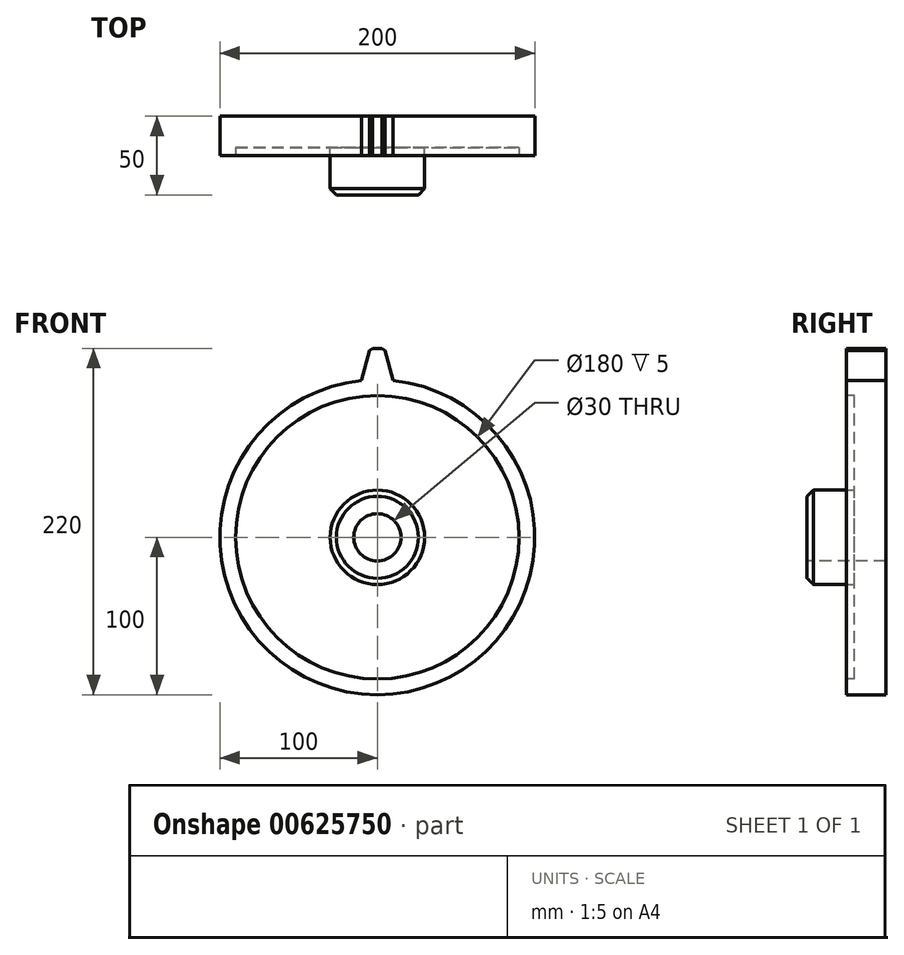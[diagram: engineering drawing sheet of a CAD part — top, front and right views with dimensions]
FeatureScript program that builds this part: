
annotation { "Feature Type Name" : "Feature", "Feature Type Description" : "" }
export const myFeature = defineFeature(function(context is Context, id is Id, definition is map)
    precondition{}
    {
        {
            var Q0;
            Q0=qCreatedBy(makeId("Front.planeOp"),FACE);
            var sketch = newSketch(context, id + "F0", { "sketchPlane" : qUnion([Q0])});
            skCircle(sketch, "E0", {"center": v(0, 0) * mm, "radius": 100 * mm});
            skSolve(sketch);
        }
        {
            var Q0;
            Q0=makeQuery(id+"F0.imprint","IMPRINT",FACE,{"disambiguationData":[TD([[makeQuery(id+"F0.imprint","IMPRINT",EDGE,{"derivedFrom":sQuery(id+"F0.wireOp",EDGE,"E0")}),1.0]])]});
            extrude(context, id + "F1", {"entities" : qUnion([Q0]), "depth" : 25 * mm, "offsetDistance" : 25 * mm});
        }
        {
            var Q0;
            Q0=makeQuery(id+"F1.opExtrude","CAP_FACE",FACE,{"disambiguationData":[OSD([sQuery(id+"F0.wireOp",EDGE,"E0")])],"isStart":false});
            var sketch = newSketch(context, id + "F2", { "sketchPlane" : qUnion([Q0])});
            skLineSegment(sketch, "E1", {"start": v(-10, 99.5) * mm, "end": v(10, 99.5) * mm});
            skLineSegment(sketch, "E2", {"start": v(10, 99.5) * mm, "end": v(4.5, 120) * mm});
            skLineSegment(sketch, "E3", {"start": v(4.5, 120) * mm, "end": v(-4.5, 120) * mm});
            skLineSegment(sketch, "E4", {"start": v(-4.5, 120) * mm, "end": v(-10, 99.5) * mm});
            skSolve(sketch);
        }
        {
            var Q0;
            {var subQ0=sQuery(id+"F2.wireOp",EDGE,"E2");Q0=makeQuery(id+"F2.imprint","IMPRINT",FACE,{"disambiguationData":[TD([[makeQuery(id+"F2.imprint","IMPRINT",EDGE,{"derivedFrom":subQ0}),1.0]])]});}
            var Q1;
            Q1 = qSketchRegion(id + "F6", true);
            var Q2;
            Q2=makeQuery(id+"F1.opExtrude","CAP_FACE",FACE,{"disambiguationData":[OSD([sQuery(id+"F0.wireOp",EDGE,"E0")])],"isStart":true});
            extrude(context, id + "F3", {"entities" : qUnion([Q0, Q1]), "operationType" : NewBodyOperationType.ADD, "endBound" : BoundingType.UP_TO_SURFACE, "oppositeDirection" : true, "depth" : 25 * mm, "endBoundEntityFace" : qUnion([Q2]), "offsetDistance" : 25 * mm});
        }
        {
            var Q0;
            Q0=makeQuery(id+"F3.opExtrude","SWEPT_EDGE",EDGE,{"disambiguationData":[OSD([sQuery(id+"F0.wireOp",EDGE,"E0"),sQuery(id+"F2.wireOp",EDGE,"E1"),sQuery(id+"F2.wireOp",EDGE,"E2")])]});
            var Q1;
            Q1=makeQuery(id+"F3.opExtrude","SWEPT_EDGE",EDGE,{"disambiguationData":[OSD([sQuery(id+"F0.wireOp",EDGE,"E0"),sQuery(id+"F2.wireOp",EDGE,"E1"),sQuery(id+"F2.wireOp",EDGE,"E4")])]});
            fillet(context, id + "F4", {"entities" : qUnion([Q0, Q1]), "radius" : 5 * mm, "tangentPropagation" : true, "allowEdgeOverflow" : false});
        }
        {
            var Q0;
            Q0=makeQuery(id+"F3.opExtrude","SWEPT_EDGE",EDGE,{"disambiguationData":[OSD([sQuery(id+"F2.wireOp",EDGE,"E2"),sQuery(id+"F2.wireOp",EDGE,"E3")])]});
            var Q1;
            Q1=makeQuery(id+"F3.opExtrude","SWEPT_EDGE",EDGE,{"disambiguationData":[OSD([sQuery(id+"F2.wireOp",EDGE,"E3"),sQuery(id+"F2.wireOp",EDGE,"E4")])]});
            chamfer(context, id + "F5", {"entities" : qUnion([Q0, Q1]), "width" : 2 * mm, "tangentPropagation" : true});
        }
        {
            var Q0;
            {var subQ0=sQuery(id+"F2.wireOp",EDGE,"E4");var subQ1=sQuery(id+"F2.wireOp",EDGE,"E3");var subQ2=sQuery(id+"F2.wireOp",EDGE,"E2");var subQ3=sQuery(id+"F0.wireOp",EDGE,"E0");Q0=makeQuery(id+"FVngeMlJqadk3JX_1.19.F3.boolean.opBoolean","MERGE",FACE,{"derivedFrom":[makeQuery(id+"FVngeMlJqadk3JX_1.18.F3.boolean.opBoolean","MERGE",FACE,{"derivedFrom":[makeQuery(id+"FVngeMlJqadk3JX_1.17.F3.boolean.opBoolean","MERGE",FACE,{"derivedFrom":[makeQuery(id+"FVngeMlJqadk3JX_1.16.F3.boolean.opBoolean","MERGE",FACE,{"derivedFrom":[makeQuery(id+"FVngeMlJqadk3JX_1.15.F3.boolean.opBoolean","MERGE",FACE,{"derivedFrom":[makeQuery(id+"FVngeMlJqadk3JX_1.14.F3.boolean.opBoolean","MERGE",FACE,{"derivedFrom":[makeQuery(id+"FVngeMlJqadk3JX_1.13.F3.boolean.opBoolean","MERGE",FACE,{"derivedFrom":[makeQuery(id+"FVngeMlJqadk3JX_1.12.F3.boolean.opBoolean","MERGE",FACE,{"derivedFrom":[makeQuery(id+"FVngeMlJqadk3JX_1.11.F3.boolean.opBoolean","MERGE",FACE,{"derivedFrom":[makeQuery(id+"FVngeMlJqadk3JX_1.10.F3.boolean.opBoolean","MERGE",FACE,{"derivedFrom":[makeQuery(id+"FVngeMlJqadk3JX_1.9.F3.boolean.opBoolean","MERGE",FACE,{"derivedFrom":[makeQuery(id+"FVngeMlJqadk3JX_1.8.F3.boolean.opBoolean","MERGE",FACE,{"derivedFrom":[makeQuery(id+"FVngeMlJqadk3JX_1.7.F3.boolean.opBoolean","MERGE",FACE,{"derivedFrom":[makeQuery(id+"FVngeMlJqadk3JX_1.6.F3.boolean.opBoolean","MERGE",FACE,{"derivedFrom":[makeQuery(id+"FVngeMlJqadk3JX_1.5.F3.boolean.opBoolean","MERGE",FACE,{"derivedFrom":[makeQuery(id+"FVngeMlJqadk3JX_1.4.F3.boolean.opBoolean","MERGE",FACE,{"derivedFrom":[makeQuery(id+"FVngeMlJqadk3JX_1.3.F3.boolean.opBoolean","MERGE",FACE,{"derivedFrom":[makeQuery(id+"FVngeMlJqadk3JX_1.2.F3.boolean.opBoolean","MERGE",FACE,{"derivedFrom":[makeQuery(id+"FVngeMlJqadk3JX_1.1.F3.boolean.opBoolean","MERGE",FACE,{"derivedFrom":[makeQuery(id+"F3.boolean.opBoolean","MERGE",FACE,{"derivedFrom":[makeQuery(id+"F1.opExtrude","CAP_FACE",FACE,{"disambiguationData":[OSD([subQ3])],"isStart":false}),makeQuery(id+"F3.opExtrude","CAP_FACE",FACE,{"disambiguationData":[OSD([subQ3,subQ2,subQ1,subQ0])],"isStart":true})]}),makeQuery(id+"FVngeMlJqadk3JX_1.1.F3.opExtrude","CAP_FACE",FACE,{"disambiguationData":[OSD([subQ3,subQ2,subQ1,subQ0])],"isStart":true})]}),makeQuery(id+"FVngeMlJqadk3JX_1.2.F3.opExtrude","CAP_FACE",FACE,{"disambiguationData":[OSD([subQ3,subQ2,subQ1,subQ0])],"isStart":true})]}),makeQuery(id+"FVngeMlJqadk3JX_1.3.F3.opExtrude","CAP_FACE",FACE,{"disambiguationData":[OSD([subQ3,subQ2,subQ1,subQ0])],"isStart":true})]}),makeQuery(id+"FVngeMlJqadk3JX_1.4.F3.opExtrude","CAP_FACE",FACE,{"disambiguationData":[OSD([subQ3,subQ2,subQ1,subQ0])],"isStart":true})]}),makeQuery(id+"FVngeMlJqadk3JX_1.5.F3.opExtrude","CAP_FACE",FACE,{"disambiguationData":[OSD([subQ3,subQ2,subQ1,subQ0])],"isStart":true})]}),makeQuery(id+"FVngeMlJqadk3JX_1.6.F3.opExtrude","CAP_FACE",FACE,{"disambiguationData":[OSD([subQ3,subQ2,subQ1,subQ0])],"isStart":true})]}),makeQuery(id+"FVngeMlJqadk3JX_1.7.F3.opExtrude","CAP_FACE",FACE,{"disambiguationData":[OSD([subQ3,subQ2,subQ1,subQ0])],"isStart":true})]}),makeQuery(id+"FVngeMlJqadk3JX_1.8.F3.opExtrude","CAP_FACE",FACE,{"disambiguationData":[OSD([subQ3,subQ2,subQ1,subQ0])],"isStart":true})]}),makeQuery(id+"FVngeMlJqadk3JX_1.9.F3.opExtrude","CAP_FACE",FACE,{"disambiguationData":[OSD([subQ3,subQ2,subQ1,subQ0])],"isStart":true})]}),makeQuery(id+"FVngeMlJqadk3JX_1.10.F3.opExtrude","CAP_FACE",FACE,{"disambiguationData":[OSD([subQ3,subQ2,subQ1,subQ0])],"isStart":true})]}),makeQuery(id+"FVngeMlJqadk3JX_1.11.F3.opExtrude","CAP_FACE",FACE,{"disambiguationData":[OSD([subQ3,subQ2,subQ1,subQ0])],"isStart":true})]}),makeQuery(id+"FVngeMlJqadk3JX_1.12.F3.opExtrude","CAP_FACE",FACE,{"disambiguationData":[OSD([subQ3,subQ2,subQ1,subQ0])],"isStart":true})]}),makeQuery(id+"FVngeMlJqadk3JX_1.13.F3.opExtrude","CAP_FACE",FACE,{"disambiguationData":[OSD([subQ3,subQ2,subQ1,subQ0])],"isStart":true})]}),makeQuery(id+"FVngeMlJqadk3JX_1.14.F3.opExtrude","CAP_FACE",FACE,{"disambiguationData":[OSD([subQ3,subQ2,subQ1,subQ0])],"isStart":true})]}),makeQuery(id+"FVngeMlJqadk3JX_1.15.F3.opExtrude","CAP_FACE",FACE,{"disambiguationData":[OSD([subQ3,subQ2,subQ1,subQ0])],"isStart":true})]}),makeQuery(id+"FVngeMlJqadk3JX_1.16.F3.opExtrude","CAP_FACE",FACE,{"disambiguationData":[OSD([subQ3,subQ2,subQ1,subQ0])],"isStart":true})]}),makeQuery(id+"FVngeMlJqadk3JX_1.17.F3.opExtrude","CAP_FACE",FACE,{"disambiguationData":[OSD([subQ3,subQ2,subQ1,subQ0])],"isStart":true})]}),makeQuery(id+"FVngeMlJqadk3JX_1.18.F3.opExtrude","CAP_FACE",FACE,{"disambiguationData":[OSD([subQ3,subQ2,subQ1,subQ0])],"isStart":true})]}),makeQuery(id+"FVngeMlJqadk3JX_1.19.F3.opExtrude","CAP_FACE",FACE,{"disambiguationData":[OSD([subQ3,subQ2,subQ1,subQ0])],"isStart":true})]});}
            var sketch = newSketch(context, id + "F6", { "sketchPlane" : qUnion([Q0])});
            skCircle(sketch, "E5", {"center": v(0, 0) * mm, "radius": 90 * mm});
            skSolve(sketch);
        }
        {
            var Q0;
            Q0=makeQuery(id+"F6.imprint","IMPRINT",FACE,{"disambiguationData":[TD([[makeQuery(id+"F6.imprint","IMPRINT",EDGE,{"derivedFrom":sQuery(id+"F6.wireOp",EDGE,"E5")}),1.0]])]});
            extrude(context, id + "F7", {"entities" : qUnion([Q0]), "operationType" : NewBodyOperationType.REMOVE, "oppositeDirection" : true, "depth" : 5 * mm, "offsetDistance" : 25 * mm});
        }
        {
            var Q0;
            Q0=makeQuery(id+"F7.boolean.opBoolean","COPY",FACE,{"derivedFrom":makeQuery(id+"F7.opExtrude","CAP_FACE",FACE,{"disambiguationData":[OSD([sQuery(id+"F6.wireOp",EDGE,"E5")])],"isStart":false})});
            var sketch = newSketch(context, id + "F8", { "sketchPlane" : qUnion([Q0])});
            skCircle(sketch, "E6", {"center": v(0, 0) * mm, "radius": 30 * mm});
            skSolve(sketch);
        }
        {
            var Q0;
            Q0=makeQuery(id+"F8.imprint","IMPRINT",FACE,{"disambiguationData":[TD([[makeQuery(id+"F8.imprint","IMPRINT",EDGE,{"derivedFrom":sQuery(id+"F8.wireOp",EDGE,"E6")}),1.0]])]});
            extrude(context, id + "F9", {"entities" : qUnion([Q0]), "operationType" : NewBodyOperationType.ADD, "depth" : 30 * mm, "offsetDistance" : 25 * mm});
        }
        {
            var Q0;
            Q0=makeQuery(id+"F9.opExtrude","CAP_FACE",FACE,{"disambiguationData":[OSD([sQuery(id+"F8.wireOp",EDGE,"E6")])],"isStart":false});
            var sketch = newSketch(context, id + "F10", { "sketchPlane" : qUnion([Q0])});
            skCircle(sketch, "E7", {"center": v(0, 0) * mm, "radius": 15 * mm});
            skSolve(sketch);
        }
        {
            var Q0;
            Q0=makeQuery(id+"F10.imprint","IMPRINT",FACE,{"disambiguationData":[TD([[makeQuery(id+"F10.imprint","IMPRINT",EDGE,{"derivedFrom":sQuery(id+"F10.wireOp",EDGE,"E7")}),1.0]])]});
            extrude(context, id + "F11", {"entities" : qUnion([Q0]), "operationType" : NewBodyOperationType.REMOVE, "endBound" : BoundingType.THROUGH_ALL, "oppositeDirection" : true, "depth" : 25 * mm, "offsetDistance" : 25 * mm});
        }
        {
            var Q0;
            Q0=makeQuery(id+"F9.opExtrude","CAP_EDGE",EDGE,{"disambiguationData":[OSD([sQuery(id+"F8.wireOp",EDGE,"E6")])],"isStart":false});
            var Q1;
            Q1=makeQuery(id+"F11.boolean.opBoolean","COPY",EDGE,{"derivedFrom":makeQuery(id+"F11.opExtrude","CAP_EDGE",EDGE,{"disambiguationData":[OSD([sQuery(id+"F10.wireOp",EDGE,"E7")])],"isStart":true})});
            chamfer(context, id + "F12", {"entities" : qUnion([Q0, Q1]), "width" : 4 * mm, "tangentPropagation" : true});
        }
    });
